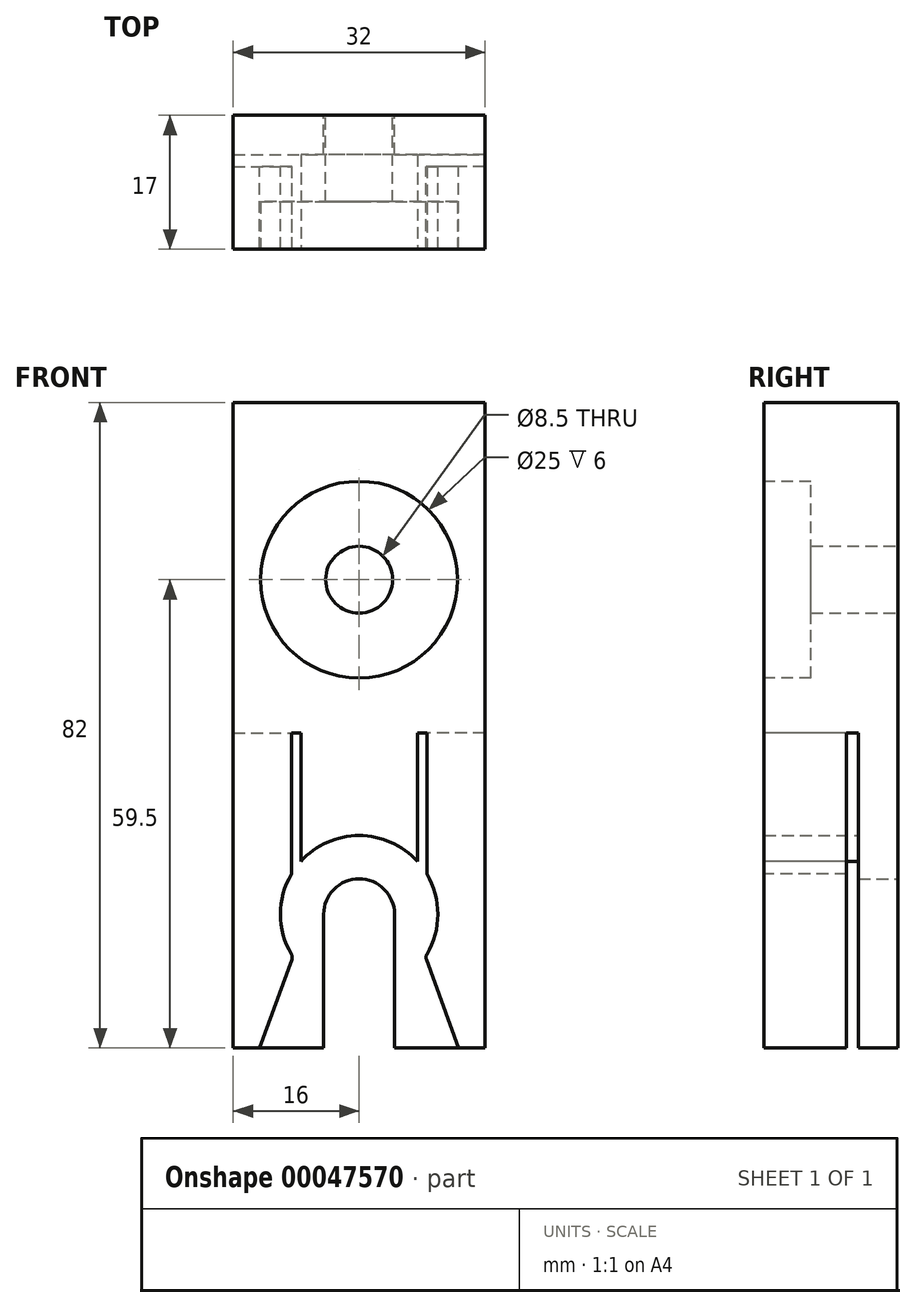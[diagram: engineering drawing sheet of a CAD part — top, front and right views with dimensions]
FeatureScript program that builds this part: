
annotation { "Feature Type Name" : "Feature", "Feature Type Description" : "" }
export const myFeature = defineFeature(function(context is Context, id is Id, definition is map)
    precondition{}
    {
        {
            var Q0;
            Q0=qCreatedBy(makeId("Front.planeOp"),FACE);
            var sketch = newSketch(context, id + "F0", { "sketchPlane" : qUnion([Q0])});
            skArc(sketch, "E0", {"start": v(8.6, -5.1) * mm, "mid": v(0, 10) * mm, "end": v(-8.6, -5.1) * mm});
            skArc(sketch, "E1", {"start": v(4.5, 0) * mm, "mid": v(0, 4.5) * mm, "end": v(-4.5, 0) * mm});
            skLineSegment(sketch, "E2.bottom", {"start": v(-16, 65) * mm, "end": v(16, 65) * mm});
            skLineSegment(sketch, "E2.top", {"start": v(-16, -17) * mm, "end": v(-4.5, -17) * mm});
            skLineSegment(sketch, "E2.left", {"start": v(-16, 65) * mm, "end": v(-16, -17) * mm});
            skLineSegment(sketch, "E2.right", {"start": v(16, 65) * mm, "end": v(16, -17) * mm});
            skLineSegment(sketch, "E3", {"start": v(-4.5, 0) * mm, "end": v(-4.5, -17) * mm});
            skLineSegment(sketch, "E4", {"start": v(4.5, 0) * mm, "end": v(4.5, -17) * mm});
            skLineSegment(sketch, "E5.trimOffspring", {"start": v(4.5, -17) * mm, "end": v(16, -17) * mm});
            skPoint(sketch, "E6.endSnap0", {"position": v(10.25, -17) * mm});
            skCircle(sketch, "E7", {"center": v(-9.25, -5.48) * mm, "radius": 0.75 * mm});
            skPoint(sketch, "E8.orphan", {"position": v(-10, 0) * mm});
            skLineSegment(sketch, "E9", {"start": v(-12.65, -17) * mm, "end": v(-8.55, -5.73) * mm});
            skCircle(sketch, "E10", {"center": v(9.25, -5.48) * mm, "radius": 0.75 * mm});
            skLineSegment(sketch, "E11", {"start": v(12.65, -17) * mm, "end": v(8.55, -5.73) * mm});
            skPoint(sketch, "E12.orphan", {"position": v(10, 0) * mm});
            skPoint(sketch, "E6.end.orphan", {"position": v(10, -17) * mm});
            skCircle(sketch, "E13", {"center": v(0, 42.5) * mm, "radius": 4.25 * mm});
            skSolve(sketch);
        }
        {
            var Q0;
            {var subQ0=sQuery(id+"F0.wireOp",EDGE,"E7");var subQ2=makeQuery(id+"F0.imprint","INTERSECT",VERTEX,{"derivedFrom":[sQuery(id+"F0.wireOp",EDGE,"E0"),subQ0]});Q0=makeQuery(id+"F0.imprint","IMPRINT",FACE,{"disambiguationData":[TD([[makeQuery(id+"F0.imprint","IMPRINT",EDGE,{"disambiguationData":[TD([[subQ2,-1.0]])],"derivedFrom":subQ0}),1.0]])]});}
            var Q1;
            {var subQ2=sQuery(id+"F0.wireOp",EDGE,"E0");Q1=makeQuery(id+"F0.imprint","IMPRINT",FACE,{"disambiguationData":[TD([[makeQuery(id+"F0.imprint","IMPRINT",EDGE,{"derivedFrom":subQ2}),-1.0]])]});}
            var Q2;
            {var subQ0=sQuery(id+"F0.wireOp",EDGE,"E10");var subQ2=makeQuery(id+"F0.imprint","INTERSECT",VERTEX,{"derivedFrom":[sQuery(id+"F0.wireOp",EDGE,"E0"),subQ0]});Q2=makeQuery(id+"F0.imprint","IMPRINT",FACE,{"disambiguationData":[TD([[makeQuery(id+"F0.imprint","IMPRINT",EDGE,{"disambiguationData":[TD([[subQ2,-1.0]])],"derivedFrom":subQ0}),1.0]])]});}
            extrude(context, id + "F1", {"entities" : qUnion([Q0, Q1, Q2]), "depth" : 17 * mm});
        }
        {
            var Q0;
            {var subQ3=sQuery(id+"F0.wireOp",EDGE,"E0");Q0=makeQuery(id+"F0.imprint","IMPRINT",FACE,{"disambiguationData":[TD([[makeQuery(id+"F0.imprint","IMPRINT",EDGE,{"derivedFrom":subQ3}),1.0]])]});}
            extrude(context, id + "F2", {"entities" : qUnion([Q0]), "operationType" : NewBodyOperationType.ADD, "depth" : 5 * mm});
        }
        {
            var Q0;
            Q0=makeQuery(id+"F1.opExtrude","CAP_FACE",FACE,{"disambiguationData":[OSD([sQuery(id+"F0.wireOp",EDGE,"E0"),sQuery(id+"F0.wireOp",EDGE,"E2.bottom"),sQuery(id+"F0.wireOp",EDGE,"E2.top"),sQuery(id+"F0.wireOp",EDGE,"E2.left"),sQuery(id+"F0.wireOp",EDGE,"E2.right"),sQuery(id+"F0.wireOp",EDGE,"E5.trimOffspring"),sQuery(id+"F0.wireOp",EDGE,"E7"),sQuery(id+"F0.wireOp",EDGE,"E9"),sQuery(id+"F0.wireOp",EDGE,"E10"),sQuery(id+"F0.wireOp",EDGE,"E11")])],"isStart":false});
            var sketch = newSketch(context, id + "F3", { "sketchPlane" : qUnion([Q0])});
            skLineSegment(sketch, "E14", {"start": v(-8.6, 5.1) * mm, "end": v(-8.6, 23) * mm});
            skLineSegment(sketch, "E15", {"start": v(-8.6, 23) * mm, "end": v(-7.4, 23) * mm});
            skLineSegment(sketch, "E16", {"start": v(-7.4, 23) * mm, "end": v(-7.4, 6.72) * mm});
            skLineSegment(sketch, "E17", {"start": v(0, 65) * mm, "end": v(0, -21.51) * mm, "construction": true});
            skPoint(sketch, "E17.endSnap0", {"position": v(0, 10) * mm});
            skLineSegment(sketch, "E18.MirrorCS", {"start": v(8.6, 5.1) * mm, "end": v(8.6, 23) * mm});
            skLineSegment(sketch, "E19.MirrorCS", {"start": v(8.6, 23) * mm, "end": v(7.4, 23) * mm});
            skLineSegment(sketch, "E20.MirrorCS", {"start": v(7.4, 23) * mm, "end": v(7.4, 6.72) * mm});
            skSolve(sketch);
        }
        {
            var Q0;
            {var subQ2=sQuery(id+"F3.wireOp",EDGE,"E14");Q0=makeQuery(id+"F3.imprint","IMPRINT",FACE,{"disambiguationData":[TD([[makeQuery(id+"F3.imprint","IMPRINT",EDGE,{"derivedFrom":subQ2}),-1.0]])]});}
            var Q1;
            {var subQ2=sQuery(id+"F3.wireOp",EDGE,"E18.MirrorCS");Q1=makeQuery(id+"F3.imprint","IMPRINT",FACE,{"disambiguationData":[TD([[makeQuery(id+"F3.imprint","IMPRINT",EDGE,{"derivedFrom":subQ2}),1.0]])]});}
            extrude(context, id + "F4", {"entities" : qUnion([Q0, Q1]), "operationType" : NewBodyOperationType.REMOVE, "oppositeDirection" : true, "depth" : 12 * mm});
        }
        {
            var Q0;
            {var subQ0=sQuery(id+"F0.wireOp",EDGE,"E2.top");Q0=makeQuery(id+"F2.boolean.opBoolean","MERGE",FACE,{"derivedFrom":[makeQuery(id+"F1.opExtrude","SWEPT_FACE",FACE,{"disambiguationData":[OSD([subQ0])]}),makeQuery(id+"F2.opExtrude","SWEPT_FACE",FACE,{"disambiguationData":[OSD([subQ0])]})]});}
            var sketch = newSketch(context, id + "F5", { "sketchPlane" : qUnion([Q0])});
            skLineSegment(sketch, "E21.bottom", {"start": v(-16, 5) * mm, "end": v(-8, 5) * mm});
            skLineSegment(sketch, "E21.top", {"start": v(-16, 6.5) * mm, "end": v(-8, 6.5) * mm});
            skLineSegment(sketch, "E21.left", {"start": v(-16, 5) * mm, "end": v(-16, 6.5) * mm});
            skLineSegment(sketch, "E21.right", {"start": v(-8, 5) * mm, "end": v(-8, 6.5) * mm});
            skLineSegment(sketch, "E22", {"start": v(0, 3.23) * mm, "end": v(0, 33.39) * mm, "construction": true});
            skLineSegment(sketch, "E23.MirrorCS", {"start": v(16, 5) * mm, "end": v(8, 5) * mm});
            skLineSegment(sketch, "E24.MirrorCS", {"start": v(16, 5) * mm, "end": v(16, 6.5) * mm});
            skLineSegment(sketch, "E25.MirrorCS", {"start": v(16, 6.5) * mm, "end": v(8, 6.5) * mm});
            skLineSegment(sketch, "E26.MirrorCS", {"start": v(8, 5) * mm, "end": v(8, 6.5) * mm});
            skSolve(sketch);
        }
        {
            var Q0;
            {var subQ6=sQuery(id+"F5.wireOp",EDGE,"E21.right");Q0=makeQuery(id+"F5.imprint","IMPRINT",FACE,{"disambiguationData":[TD([[makeQuery(id+"F5.imprint","IMPRINT",EDGE,{"derivedFrom":subQ6}),1.0]])]});}
            var Q1;
            {var subQ6=sQuery(id+"F5.wireOp",EDGE,"E21.left");Q1=makeQuery(id+"F5.imprint","IMPRINT",FACE,{"disambiguationData":[TD([[makeQuery(id+"F5.imprint","IMPRINT",EDGE,{"derivedFrom":subQ6}),1.0]])]});}
            var Q2;
            Q2=makeQuery(id+"F5.imprint","IMPRINT",FACE,{"disambiguationData":[TD([[makeQuery(id+"F5.imprint","IMPRINT",EDGE,{"derivedFrom":sQuery(id+"F5.wireOp",EDGE,"E23.MirrorCS")}),-1.0]])]});
            var Q3;
            Q3 = qSketchRegion(id + "F7", true);
            extrude(context, id + "F6", {"entities" : qUnion([Q0, Q1, Q2, Q3]), "operationType" : NewBodyOperationType.REMOVE, "oppositeDirection" : true, "depth" : 40 * mm});
        }
        {
            var Q0;
            Q0=makeQuery(id+"F1.opExtrude","CAP_FACE",FACE,{"disambiguationData":[OSD([sQuery(id+"F0.wireOp",EDGE,"E0"),sQuery(id+"F0.wireOp",EDGE,"E2.bottom"),sQuery(id+"F0.wireOp",EDGE,"E2.top"),sQuery(id+"F0.wireOp",EDGE,"E2.left"),sQuery(id+"F0.wireOp",EDGE,"E2.right"),sQuery(id+"F0.wireOp",EDGE,"E5.trimOffspring"),sQuery(id+"F0.wireOp",EDGE,"E7"),sQuery(id+"F0.wireOp",EDGE,"E9"),sQuery(id+"F0.wireOp",EDGE,"E10"),sQuery(id+"F0.wireOp",EDGE,"E11"),sQuery(id+"F0.wireOp",EDGE,"E13")])],"isStart":false});
            var sketch = newSketch(context, id + "F7", { "sketchPlane" : qUnion([Q0])});
            skCircle(sketch, "E27", {"center": v(0, 42.5) * mm, "radius": 12.5 * mm});
            skSolve(sketch);
        }
        {
            var Q0;
            Q0=makeQuery(id+"F7.imprint","IMPRINT",FACE,{"disambiguationData":[TD([[makeQuery(id+"F7.imprint","IMPRINT",EDGE,{"derivedFrom":sQuery(id+"F7.wireOp",EDGE,"E27")}),1.0]])]});
            extrude(context, id + "F8", {"entities" : qUnion([Q0]), "operationType" : NewBodyOperationType.REMOVE, "oppositeDirection" : true, "depth" : 6 * mm});
        }
    });
